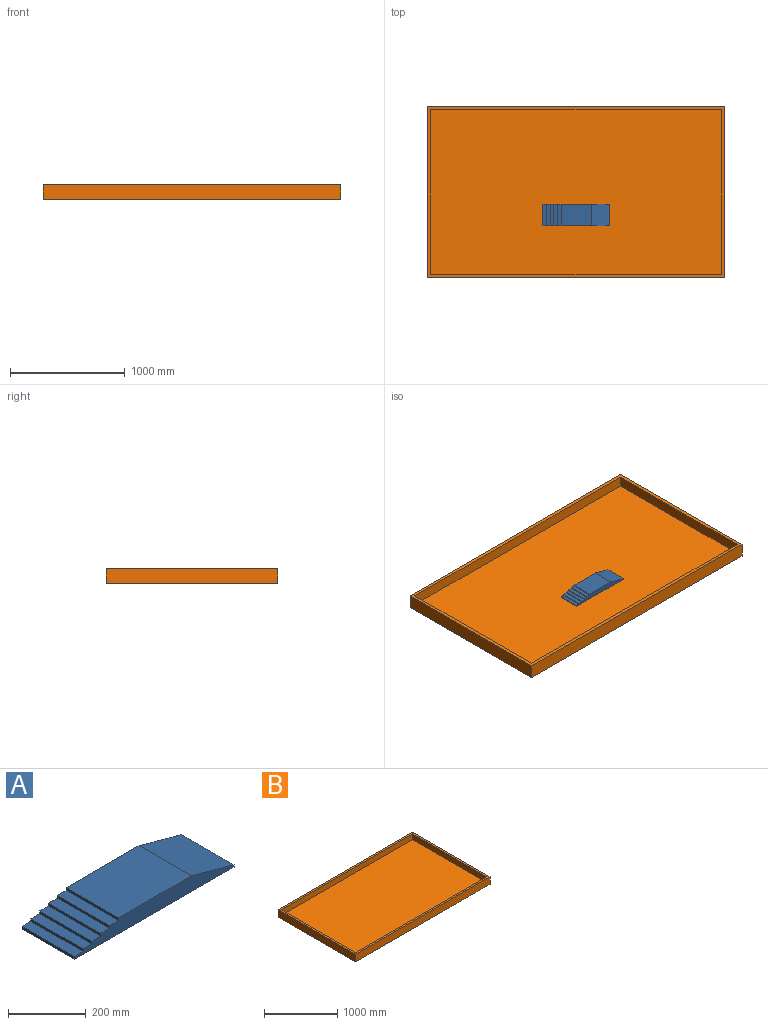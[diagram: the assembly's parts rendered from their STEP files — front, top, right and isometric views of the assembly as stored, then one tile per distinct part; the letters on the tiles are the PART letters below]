
ASSEMBLY  parts=2 mates=1
PART A: 17 faces, bbox 580x190x50 mm
  f0: plane 580x50mm, normal (0,1,0), area 21677.1mm2, adj f1,f3,f4,f5,f6,f7,f8,f9
  f1: plane 190x7mm, normal (1,0,0), area 1330mm2, adj f0,f2,f5,f16
  f2: plane 580x50mm, normal (0,-1,0), area 21677.1mm2, adj f1,f3,f4,f5,f6,f7,f8,f9
  f3: plane 190x8.4mm, normal (-1,0,0), area 1596mm2, adj f0,f2,f5,f15
  f4: plane 265x190mm, normal (0,0,1), area 50350mm2, adj f0,f2,f6,f16
  f5: plane 580x190mm, normal (0,0,-1), area 110200mm2, adj f0,f1,f2,f3
  f6: plane 190x8.3mm, normal (-1,0,0), area 1577mm2, adj f0,f2,f4,f7
  f7: plane 190x32mm, normal (0,0,1), area 6080mm2, adj f0,f2,f6,f8
  f8: plane 190x8.3mm, normal (-1,0,0), area 1577mm2, adj f0,f2,f7,f9
  f9: plane 190x32mm, normal (0,0,1), area 6080mm2, adj f0,f2,f8,f10
  f10: plane 190x8.3mm, normal (-1,0,0), area 1577mm2, adj f0,f2,f9,f11
  f11: plane 190x32mm, normal (0,0,1), area 6080mm2, adj f0,f2,f10,f12
  f12: plane 190x8.4mm, normal (-1,0,0), area 1596mm2, adj f0,f2,f11,f13
  f13: plane 190x32mm, normal (0,0,1), area 6080mm2, adj f0,f2,f12,f14
  f14: plane 190x8.3mm, normal (-1,0,0), area 1577mm2, adj f0,f2,f13,f15
  f15: plane 190x32mm, normal (0,0,1), area 6080mm2, adj f0,f2,f3,f14
  f16: plane 190x155mm, normal (0.27,0,0.96), area 30562.3mm2, adj f0,f1,f2,f4
PART B: 11 faces, bbox 2600x1500x125 mm
  f0: plane 2600x125mm, normal (0,1,0), area 325000mm2, adj f1,f3,f4,f5
  f1: plane 1500x125mm, normal (-1,0,0), area 187500mm2, adj f0,f2,f4,f5
  f2: plane 2600x125mm, normal (0,-1,0), area 325000mm2, adj f1,f3,f4,f5
  f3: plane 1500x125mm, normal (1,0,0), area 187500mm2, adj f0,f2,f4,f5
  f4: plane 2600x1500mm, normal (0,0,1), area 242400mm2, adj f0,f1,f2,f3,f6,f7,f8,f9
  f5: plane 2600x1500mm, normal (0,0,-1), area 3900000mm2, adj f0,f1,f2,f3
  f6: plane 2540x95mm, normal (0,-1,0), area 241300mm2, adj f4,f7,f9,f10
  f7: plane 1440x95mm, normal (1,0,0), area 136800mm2, adj f4,f6,f8,f10
  f8: plane 2540x95mm, normal (0,1,0), area 241300mm2, adj f4,f7,f9,f10
  f9: plane 1440x95mm, normal (-1,0,0), area 136800mm2, adj f4,f6,f8,f10
  f10: plane 2540x1440mm, normal (0,0,1), area 3657600mm2, adj f6,f7,f8,f9
PLACE A t=(0,-200,30)mm
PLACE B at identity
MATE parallel A.f5 <-> B.f10  axis (0,0,-1) through (0,-200,30)mm
